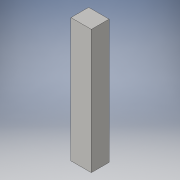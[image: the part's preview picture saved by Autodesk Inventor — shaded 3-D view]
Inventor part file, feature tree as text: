
AUTODESK INVENTOR PART (.ipt)
format: ipt  version: 2016 (Build 200138000, 138)  size: 87,040 bytes
history: native  units: in
note: dims shown in document units (in); Inventor stores cm internally (conversion verified against a paired STEP export)
features: extrude x1, sketch x1
ambient origin geometry x8: Origin, YZ Plane, XZ Plane, XY Plane, X Axis, Y Axis, Z Axis, Center Point
bodies: Solid1 (feature_tree)
feature tree (2):
  extrude  "Extrusion1"  Depth=14.0in
  sketch  "Sketch1"  dims[d0=2.3in d1=14.0in d2=2.0in d3=0.0in]
